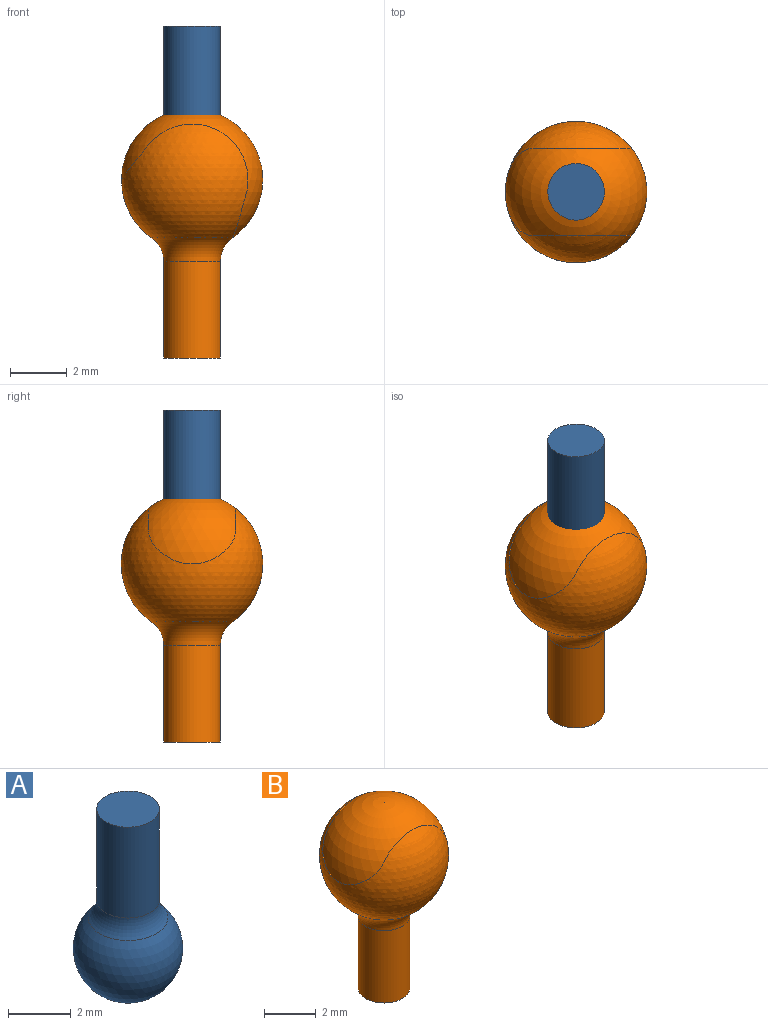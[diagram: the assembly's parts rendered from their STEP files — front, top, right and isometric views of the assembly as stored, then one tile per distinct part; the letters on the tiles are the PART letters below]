
ASSEMBLY  parts=2 mates=1
PART A: 4 faces, bbox 3.5x3.5x7.2 mm
  f0: cylinder r=1mm len=3.55mm, axis (0,0,-1), area 22.3mm2, adj f2,f3
  f1: sphere r=1.75mm, area 32.4mm2, adj f3
  f2: plane 2x2mm, normal (0,0,1), area 3.1mm2, adj f0
  f3: torus R=2mm, axis (0,0,-1), area 5.2mm2, adj f0,f1
PART B: 22 faces, bbox 6x5x8.8 mm
  f0: sphere r=2.5mm, area 42mm2, adj f1,f13,f14,f15,f16,f17,f18,f21
  f1: cone r=1.44mm half-angle=45deg, axis (0,1,0), area 1.3mm2, adj f0,f2,f13,f21
  f2: torus R=1.45mm, axis (0,-1,0), area 3.1mm2, adj f1,f3,f11,f12
  f3: sphere r=1.75mm, area 18.6mm2, adj f2,f4,f5,f6,f7,f10,f11,f12
  f4: bspline ~1.66x1.41mm, area 1.3mm2, adj f3,f5,f10,f15
  f5: torus R=1.45mm, axis (0,1,0), area 3.1mm2, adj f3,f4,f6,f16
  f6: bspline ~1.52x1.49mm, area 1.3mm2, adj f3,f5,f7,f17
  f7: torus R=2.19mm, axis (-0.82,0,-0.57), area 0mm2, adj f3,f6,f8,f12
  f8: plane 0.25x0.18mm, normal (-0.82,0,-0.57), area 0mm2, adj f7,f9,f17,f21
  f9: sphere r=2.5mm, area 78.5mm2, adj f8,f18
  f10: torus R=2.19mm, axis (0,0,1), area 0mm2, adj f3,f4,f11,f14
  f11: bspline ~1.52x1.52mm, area 1.3mm2, adj f2,f3,f10,f13
  f12: bspline ~1.49x1.38mm, area 1.3mm2, adj f2,f3,f7,f21
  f13: bspline ~2.52x2.06mm, area 0.6mm2, adj f0,f1,f11,f14
  f14: plane 0.31x0.07mm, normal (0,0,-1), area 0mm2, adj f0,f10,f13,f15
  f15: bspline ~2.52x2.06mm, area 0.6mm2, adj f0,f4,f14,f16
  f16: cone r=1.44mm half-angle=45deg, axis (0,-1,0), area 1.3mm2, adj f0,f5,f15,f17
  f17: bspline ~2.44x2.06mm, area 0.6mm2, adj f0,f6,f8,f16
  f18: torus R=2mm, axis (0,0,1), area 6.9mm2, adj f0,f9,f19
  f19: cylinder r=1mm len=3.42mm, axis (0,0,1), area 21.5mm2, adj f18,f20
  f20: plane 2x2mm, normal (0,0,1), area 3.1mm2, adj f19
  f21: bspline ~2.44x2.06mm, area 0.6mm2, adj f0,f1,f8,f12
PLACE A at identity
PLACE B at identity fixed
MATE ball A.f3 <-> B.f10  axis (0,0,1) through (0,0,0)mm
